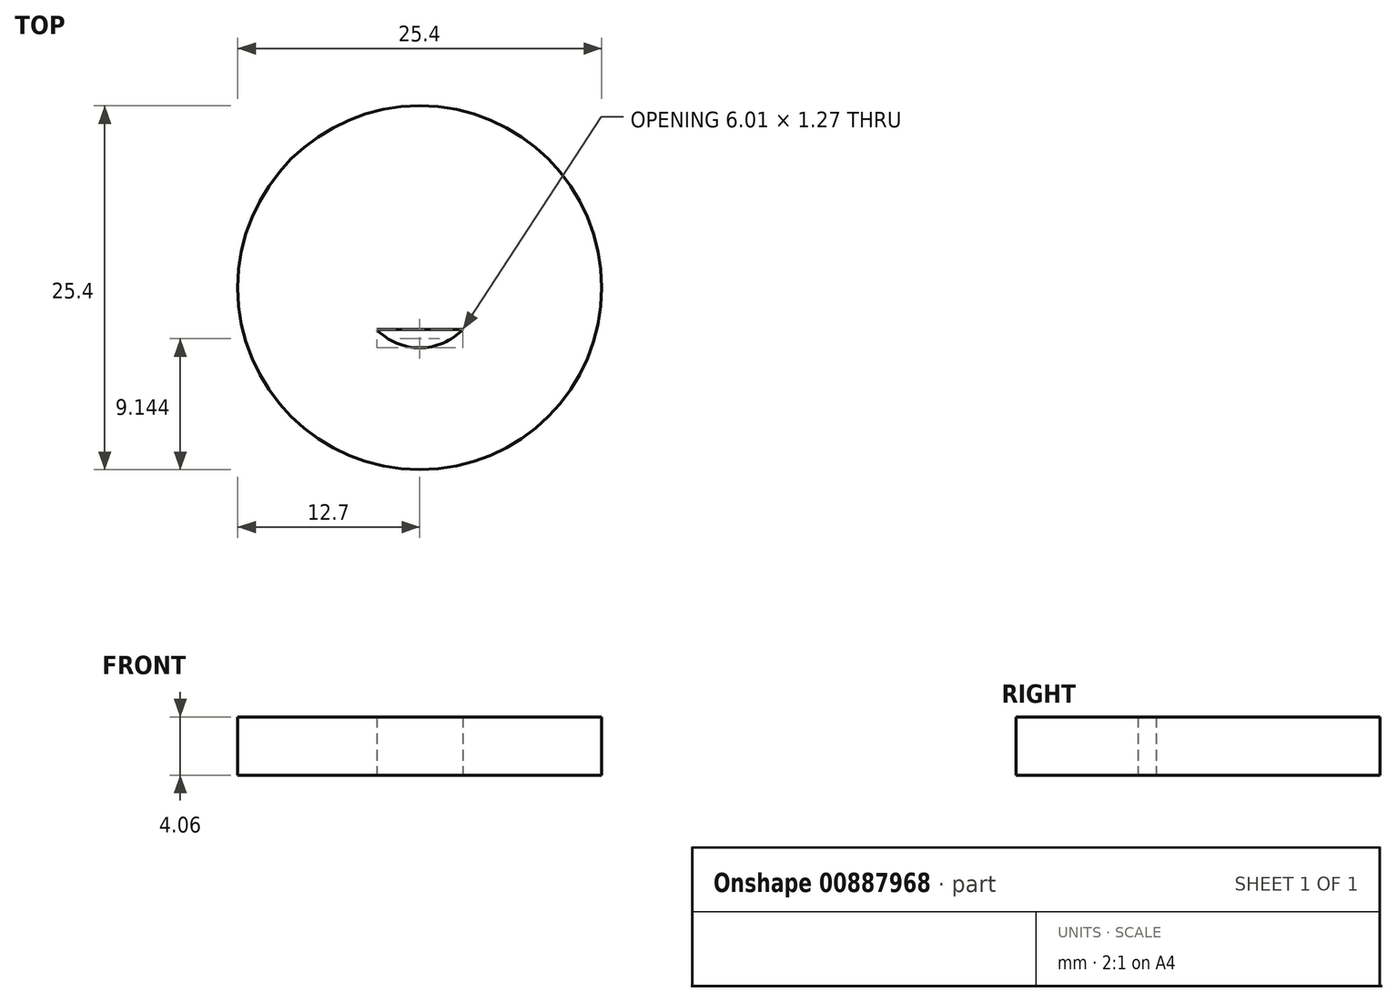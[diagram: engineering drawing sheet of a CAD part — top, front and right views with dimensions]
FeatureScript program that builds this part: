
annotation { "Feature Type Name" : "Feature", "Feature Type Description" : "" }
export const myFeature = defineFeature(function(context is Context, id is Id, definition is map)
    precondition{}
    {
        {
            var Q0;
            Q0=qCreatedBy(makeId("Top.planeOp"),FACE);
            var sketch = newSketch(context, id + "F0", { "sketchPlane" : qUnion([Q0])});
            skCircle(sketch, "E0", {"center": v(0, 0) * mm, "radius": 4.2 * mm});
            skCircle(sketch, "E1", {"center": v(0, 0) * mm, "radius": 12.7 * mm});
            skLineSegment(sketch, "E2", {"start": v(0, 4.2) * mm, "end": v(17.1, 4.2) * mm});
            skLineSegment(sketch, "E3.0", {"start": v(-5.5, -2.92) * mm, "end": v(17.1, -2.92) * mm});
            skSolve(sketch);
        }
        {
            var Q0;
            {var subQ0=sQuery(id+"F0.wireOp",EDGE,"E2");var subQ5=sQuery(id+"F0.wireOp",EDGE,"E0");var subQ8=makeQuery(id+"F0.imprint","INTERSECT",VERTEX,{"derivedFrom":[subQ5,subQ0]});Q0=makeQuery(id+"F0.imprint","IMPRINT",FACE,{"disambiguationData":[TD([[makeQuery(id+"F0.imprint","IMPRINT",EDGE,{"disambiguationData":[TD([[subQ8,-1.0]])],"derivedFrom":subQ5}),-1.0]])]});}
            var Q1;
            {var subQ0=sQuery(id+"F0.wireOp",EDGE,"E2");var subQ1=sQuery(id+"F0.wireOp",EDGE,"E0");var subQ2=makeQuery(id+"F0.imprint","INTERSECT",VERTEX,{"derivedFrom":[subQ1,subQ0]});Q1=makeQuery(id+"F0.imprint","IMPRINT",FACE,{"disambiguationData":[TD([[makeQuery(id+"F0.imprint","IMPRINT",EDGE,{"disambiguationData":[TD([[subQ2,1.0]])],"derivedFrom":subQ1}),-1.0]])]});}
            var Q2;
            {var subQ0=sQuery(id+"F0.wireOp",EDGE,"E3.0");var subQ1=sQuery(id+"F0.wireOp",EDGE,"E0");var subQ2=makeQuery(id+"F0.imprint","INTERSECT",VERTEX,{"disambiguationData":[OD(0.0)],"derivedFrom":[subQ1,subQ0]});Q2=makeQuery(id+"F0.imprint","IMPRINT",FACE,{"disambiguationData":[TD([[makeQuery(id+"F0.imprint","IMPRINT",EDGE,{"disambiguationData":[TD([[subQ2,-1.0]])],"derivedFrom":subQ1}),1.0]])]});}
            extrude(context, id + "F1", {"entities" : qUnion([Q0, Q1, Q2]), "depth" : 4.06 * mm, "offsetDistance" : 25.4 * mm});
        }
    });
